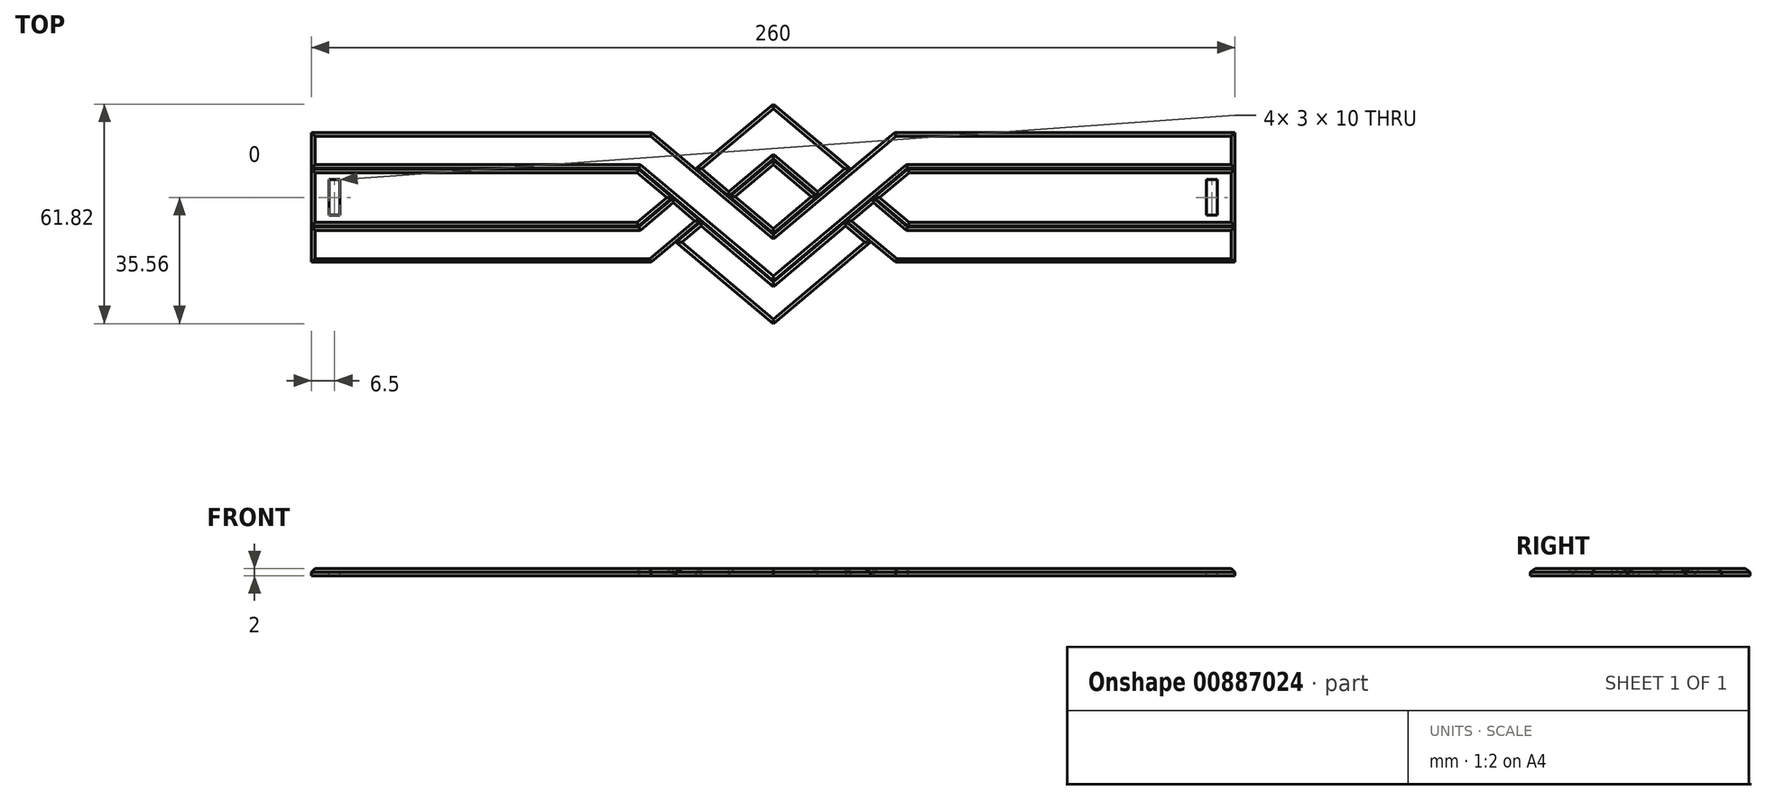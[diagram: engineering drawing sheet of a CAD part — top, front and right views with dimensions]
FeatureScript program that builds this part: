
annotation { "Feature Type Name" : "Feature", "Feature Type Description" : "" }
export const myFeature = defineFeature(function(context is Context, id is Id, definition is map)
    precondition{}
    {
        {
            var Q0;
            Q0=qCreatedBy(makeId("Top.planeOp"),FACE);
            var sketch = newSketch(context, id + "F0", { "sketchPlane" : qUnion([Q0])});
            skLineSegment(sketch, "E0", {"start": v(28.38, 0) * mm, "end": v(37.92, 8) * mm});
            skLineSegment(sketch, "E1", {"start": v(37.92, 8) * mm, "end": v(130, 8) * mm});
            skLineSegment(sketch, "E2", {"start": v(130, 8) * mm, "end": v(130, 0) * mm});
            skLineSegment(sketch, "E3.MirrorCS", {"start": v(28.38, 0) * mm, "end": v(37.92, -8) * mm});
            skLineSegment(sketch, "E4.MirrorCS", {"start": v(37.92, -8) * mm, "end": v(130, -8) * mm});
            skLineSegment(sketch, "E5.MirrorCS", {"start": v(130, -8) * mm, "end": v(130, 0) * mm});
            skLineSegment(sketch, "E6.MirrorCS", {"start": v(-28.38, 0) * mm, "end": v(-37.92, 8) * mm});
            skLineSegment(sketch, "E7.MirrorCS", {"start": v(-37.92, -8) * mm, "end": v(-130, -8) * mm});
            skLineSegment(sketch, "E8.MirrorCS", {"start": v(-28.38, 0) * mm, "end": v(-37.92, -8) * mm});
            skLineSegment(sketch, "E9.MirrorCS", {"start": v(-37.92, 8) * mm, "end": v(-130, 8) * mm});
            skLineSegment(sketch, "E10.MirrorCS", {"start": v(-130, -8) * mm, "end": v(-130, 0) * mm});
            skLineSegment(sketch, "E11.MirrorCS", {"start": v(-130, 8) * mm, "end": v(-130, 0) * mm});
            skSolve(sketch);
        }
        {
            var Q0;
            Q0 = qSketchRegion(id + "F0", true);
            extrude(context, id + "F1", {"entities" : qUnion([Q0]), "depth" : 2 * mm, "offsetDistance" : 25 * mm});
        }
        {
            var Q0;
            Q0=qCreatedBy(makeId("Top.planeOp"),FACE);
            var sketch = newSketch(context, id + "F2", { "sketchPlane" : qUnion([Q0])});
            skLineSegment(sketch, "E12", {"start": v(0, -23.49) * mm, "end": v(37.82, 8.25) * mm});
            skLineSegment(sketch, "E13", {"start": v(37.82, 8.25) * mm, "end": v(130, 8.25) * mm});
            skLineSegment(sketch, "E14", {"start": v(130, 8.25) * mm, "end": v(130, 18.25) * mm});
            skLineSegment(sketch, "E15", {"start": v(130, 18.25) * mm, "end": v(34.18, 18.25) * mm});
            skLineSegment(sketch, "E16", {"start": v(34.18, 18.25) * mm, "end": v(0, -10.43) * mm});
            skLineSegment(sketch, "E17.MirrorCS", {"start": v(-130, 8.25) * mm, "end": v(-130, 18.25) * mm});
            skLineSegment(sketch, "E18.MirrorCS", {"start": v(-130, 18.25) * mm, "end": v(-34.18, 18.25) * mm});
            skLineSegment(sketch, "E19.MirrorCS", {"start": v(0, -23.49) * mm, "end": v(-37.82, 8.25) * mm});
            skLineSegment(sketch, "E20.MirrorCS", {"start": v(-34.18, 18.25) * mm, "end": v(0, -10.43) * mm});
            skLineSegment(sketch, "E21.MirrorCS", {"start": v(-37.82, 8.25) * mm, "end": v(-130, 8.25) * mm});
            skSolve(sketch);
        }
        {
            var Q0;
            Q0 = qSketchRegion(id + "F2", true);
            extrude(context, id + "F3", {"entities" : qUnion([Q0]), "depth" : 2 * mm, "offsetDistance" : 25 * mm});
        }
        {
            var Q0;
            Q0=qCreatedBy(makeId("Top.planeOp"),FACE);
            var sketch = newSketch(context, id + "F4", { "sketchPlane" : qUnion([Q0])});
            skLineSegment(sketch, "E22", {"start": v(21.67, 8.08) * mm, "end": v(12.48, 0.37) * mm});
            skLineSegment(sketch, "E23", {"start": v(12.48, 0.37) * mm, "end": v(0, 10.84) * mm});
            skLineSegment(sketch, "E24", {"start": v(21.67, 8.08) * mm, "end": v(0, 26.26) * mm});
            skLineSegment(sketch, "E25", {"start": v(28.19, -0.16) * mm, "end": v(37.82, -8.25) * mm});
            skLineSegment(sketch, "E26", {"start": v(37.82, -8.25) * mm, "end": v(130, -8.25) * mm});
            skLineSegment(sketch, "E27", {"start": v(130, -8.25) * mm, "end": v(130, -18.25) * mm});
            skLineSegment(sketch, "E28", {"start": v(130, -18.25) * mm, "end": v(34.42, -18.25) * mm});
            skLineSegment(sketch, "E29", {"start": v(34.42, -18.25) * mm, "end": v(20.53, -6.6) * mm});
            skLineSegment(sketch, "E30", {"start": v(20.53, -6.6) * mm, "end": v(28.19, -0.16) * mm});
            skLineSegment(sketch, "E31.MirrorCS", {"start": v(-21.67, 8.08) * mm, "end": v(-12.48, 0.37) * mm});
            skLineSegment(sketch, "E32.MirrorCS", {"start": v(-21.67, 8.08) * mm, "end": v(0, 26.26) * mm});
            skLineSegment(sketch, "E33.MirrorCS", {"start": v(-12.48, 0.37) * mm, "end": v(0, 10.84) * mm});
            skLineSegment(sketch, "E34.MirrorCS", {"start": v(-34.42, -18.25) * mm, "end": v(-20.53, -6.6) * mm});
            skLineSegment(sketch, "E35.MirrorCS", {"start": v(-28.19, -0.16) * mm, "end": v(-37.82, -8.25) * mm});
            skLineSegment(sketch, "E36.MirrorCS", {"start": v(-130, -18.25) * mm, "end": v(-34.42, -18.25) * mm});
            skLineSegment(sketch, "E37.MirrorCS", {"start": v(-20.53, -6.6) * mm, "end": v(-28.19, -0.16) * mm});
            skLineSegment(sketch, "E38.MirrorCS", {"start": v(-37.82, -8.25) * mm, "end": v(-130, -8.25) * mm});
            skLineSegment(sketch, "E39.MirrorCS", {"start": v(-130, -8.25) * mm, "end": v(-130, -18.25) * mm});
            skSolve(sketch);
        }
        {
            var Q0;
            Q0 = qSketchRegion(id + "F4", true);
            extrude(context, id + "F5", {"entities" : qUnion([Q0]), "depth" : 2 * mm, "offsetDistance" : 25 * mm});
        }
        {
            var Q0;
            Q0=qCreatedBy(makeId("Top.planeOp"),FACE);
            var sketch = newSketch(context, id + "F6", { "sketchPlane" : qUnion([Q0])});
            skLineSegment(sketch, "E40", {"start": v(0, -35.56) * mm, "end": v(27.33, -12.63) * mm});
            skLineSegment(sketch, "E41", {"start": v(27.33, -12.63) * mm, "end": v(20.33, -6.75) * mm});
            skLineSegment(sketch, "E42", {"start": v(20.33, -6.75) * mm, "end": v(0, -23.81) * mm});
            skLineSegment(sketch, "E43", {"start": v(0, -10.1) * mm, "end": v(12.29, 0.2) * mm});
            skLineSegment(sketch, "E44", {"start": v(12.29, 0.2) * mm, "end": v(0, 10.51) * mm});
            skLineSegment(sketch, "E45.MirrorCS", {"start": v(-12.29, 0.2) * mm, "end": v(0, 10.51) * mm});
            skLineSegment(sketch, "E46.MirrorCS", {"start": v(0, -35.56) * mm, "end": v(-27.33, -12.63) * mm});
            skLineSegment(sketch, "E47.MirrorCS", {"start": v(0, -10.1) * mm, "end": v(-12.29, 0.2) * mm});
            skLineSegment(sketch, "E48.MirrorCS", {"start": v(-27.33, -12.63) * mm, "end": v(-20.33, -6.75) * mm});
            skLineSegment(sketch, "E49.MirrorCS", {"start": v(-20.33, -6.75) * mm, "end": v(0, -23.81) * mm});
            skSolve(sketch);
        }
        {
            var Q0;
            Q0 = qSketchRegion(id + "F6", true);
            extrude(context, id + "F7", {"entities" : qUnion([Q0]), "depth" : 2 * mm, "offsetDistance" : 25 * mm});
        }
        {
            var Q0;
            Q0=qCreatedBy(makeId("Top.planeOp"),FACE);
            var sketch = newSketch(context, id + "F8", { "sketchPlane" : qUnion([Q0])});
            skLineSegment(sketch, "E50", {"start": v(0, 26.26) * mm, "end": v(21.87, 7.92) * mm});
            skLineSegment(sketch, "E51", {"start": v(21.87, 7.92) * mm, "end": v(34.18, 18.25) * mm});
            skLineSegment(sketch, "E52", {"start": v(34.18, 18.25) * mm, "end": v(130, 18.25) * mm});
            skLineSegment(sketch, "E53", {"start": v(130, 18.25) * mm, "end": v(130, -18.25) * mm});
            skLineSegment(sketch, "E54", {"start": v(130, -18.25) * mm, "end": v(34.42, -18.25) * mm});
            skLineSegment(sketch, "E55", {"start": v(34.42, -18.25) * mm, "end": v(27.53, -12.47) * mm});
            skLineSegment(sketch, "E56", {"start": v(27.53, -12.47) * mm, "end": v(0, -35.56) * mm});
            skLineSegment(sketch, "E57.MirrorCS", {"start": v(-130, 18.25) * mm, "end": v(-130, -18.25) * mm});
            skLineSegment(sketch, "E58.MirrorCS", {"start": v(0, 26.26) * mm, "end": v(-21.87, 7.92) * mm});
            skLineSegment(sketch, "E59.MirrorCS", {"start": v(-34.18, 18.25) * mm, "end": v(-130, 18.25) * mm});
            skLineSegment(sketch, "E60.MirrorCS", {"start": v(-130, -18.25) * mm, "end": v(-34.42, -18.25) * mm});
            skLineSegment(sketch, "E61.MirrorCS", {"start": v(-34.42, -18.25) * mm, "end": v(-27.53, -12.47) * mm});
            skLineSegment(sketch, "E62.MirrorCS", {"start": v(-21.87, 7.92) * mm, "end": v(-34.18, 18.25) * mm});
            skLineSegment(sketch, "E63.MirrorCS", {"start": v(-27.53, -12.47) * mm, "end": v(0, -35.56) * mm});
            skSolve(sketch);
        }
        {
            var Q0;
            Q0 = qSketchRegion(id + "F8", true);
            extrude(context, id + "F9", {"entities" : qUnion([Q0]), "depth" : 1 * mm, "offsetDistance" : 25 * mm});
        }
        {
            var Q0;
            Q0=makeQuery(id+"F3.opExtrude","CAP_FACE",FACE,{"disambiguationData":[OSD([sQuery(id+"F2.wireOp",EDGE,"E12"),sQuery(id+"F2.wireOp",EDGE,"E13"),sQuery(id+"F2.wireOp",EDGE,"E14"),sQuery(id+"F2.wireOp",EDGE,"E15"),sQuery(id+"F2.wireOp",EDGE,"E16"),sQuery(id+"F2.wireOp",EDGE,"E17.MirrorCS"),sQuery(id+"F2.wireOp",EDGE,"E18.MirrorCS"),sQuery(id+"F2.wireOp",EDGE,"E19.MirrorCS"),sQuery(id+"F2.wireOp",EDGE,"E20.MirrorCS"),sQuery(id+"F2.wireOp",EDGE,"E21.MirrorCS")])],"isStart":false});
            var Q1;
            Q1=makeQuery(id+"F1.opExtrude","CAP_FACE",FACE,{"disambiguationData":[OSD([sQuery(id+"F0.wireOp",EDGE,"E6.MirrorCS"),sQuery(id+"F0.wireOp",EDGE,"E7.MirrorCS"),sQuery(id+"F0.wireOp",EDGE,"E8.MirrorCS"),sQuery(id+"F0.wireOp",EDGE,"E9.MirrorCS"),sQuery(id+"F0.wireOp",EDGE,"E10.MirrorCS"),sQuery(id+"F0.wireOp",EDGE,"E11.MirrorCS")])],"isStart":false});
            var Q2;
            Q2=makeQuery(id+"F5.opExtrude","CAP_FACE",FACE,{"disambiguationData":[OSD([sQuery(id+"F4.wireOp",EDGE,"E34.MirrorCS"),sQuery(id+"F4.wireOp",EDGE,"E35.MirrorCS"),sQuery(id+"F4.wireOp",EDGE,"E36.MirrorCS"),sQuery(id+"F4.wireOp",EDGE,"E37.MirrorCS"),sQuery(id+"F4.wireOp",EDGE,"E38.MirrorCS"),sQuery(id+"F4.wireOp",EDGE,"E39.MirrorCS")])],"isStart":false});
            var Q3;
            Q3=makeQuery(id+"F5.opExtrude","CAP_FACE",FACE,{"disambiguationData":[OSD([sQuery(id+"F4.wireOp",EDGE,"E22"),sQuery(id+"F4.wireOp",EDGE,"E23"),sQuery(id+"F4.wireOp",EDGE,"E24"),sQuery(id+"F4.wireOp",EDGE,"E31.MirrorCS"),sQuery(id+"F4.wireOp",EDGE,"E32.MirrorCS"),sQuery(id+"F4.wireOp",EDGE,"E33.MirrorCS")])],"isStart":false});
            var Q4;
            Q4=makeQuery(id+"F7.opExtrude","CAP_FACE",FACE,{"disambiguationData":[OSD([sQuery(id+"F6.wireOp",EDGE,"E43"),sQuery(id+"F6.wireOp",EDGE,"E44"),sQuery(id+"F6.wireOp",EDGE,"E45.MirrorCS"),sQuery(id+"F6.wireOp",EDGE,"E47.MirrorCS")])],"isStart":false});
            var Q5;
            Q5=makeQuery(id+"F7.opExtrude","CAP_FACE",FACE,{"disambiguationData":[OSD([sQuery(id+"F6.wireOp",EDGE,"E40"),sQuery(id+"F6.wireOp",EDGE,"E41"),sQuery(id+"F6.wireOp",EDGE,"E42"),sQuery(id+"F6.wireOp",EDGE,"E46.MirrorCS"),sQuery(id+"F6.wireOp",EDGE,"E48.MirrorCS"),sQuery(id+"F6.wireOp",EDGE,"E49.MirrorCS")])],"isStart":false});
            var Q6;
            Q6=makeQuery(id+"F5.opExtrude","CAP_FACE",FACE,{"disambiguationData":[OSD([sQuery(id+"F4.wireOp",EDGE,"E25"),sQuery(id+"F4.wireOp",EDGE,"E26"),sQuery(id+"F4.wireOp",EDGE,"E27"),sQuery(id+"F4.wireOp",EDGE,"E28"),sQuery(id+"F4.wireOp",EDGE,"E29"),sQuery(id+"F4.wireOp",EDGE,"E30")])],"isStart":false});
            var Q7;
            Q7=makeQuery(id+"F1.opExtrude","CAP_FACE",FACE,{"disambiguationData":[OSD([sQuery(id+"F0.wireOp",EDGE,"E0"),sQuery(id+"F0.wireOp",EDGE,"E1"),sQuery(id+"F0.wireOp",EDGE,"E2"),sQuery(id+"F0.wireOp",EDGE,"E3.MirrorCS"),sQuery(id+"F0.wireOp",EDGE,"E4.MirrorCS"),sQuery(id+"F0.wireOp",EDGE,"E5.MirrorCS")])],"isStart":false});
            chamfer(context, id + "F10", {"entities" : qUnion([Q0, Q1, Q2, Q3, Q4, Q5, Q6, Q7]), "width" : 1 * mm, "tangentPropagation" : true});
        }
        {
            var Q0;
            Q0=makeQuery(id+"F1.opExtrude","CAP_FACE",FACE,{"disambiguationData":[OSD([sQuery(id+"F0.wireOp",EDGE,"E0"),sQuery(id+"F0.wireOp",EDGE,"E1"),sQuery(id+"F0.wireOp",EDGE,"E2"),sQuery(id+"F0.wireOp",EDGE,"E3.MirrorCS"),sQuery(id+"F0.wireOp",EDGE,"E4.MirrorCS"),sQuery(id+"F0.wireOp",EDGE,"E5.MirrorCS")])],"isStart":false});
            var sketch = newSketch(context, id + "F11", { "sketchPlane" : qUnion([Q0])});
            skLineSegment(sketch, "E64.bottom", {"start": v(122, 5) * mm, "end": v(125, 5) * mm});
            skLineSegment(sketch, "E64.top", {"start": v(122, -5) * mm, "end": v(125, -5) * mm});
            skLineSegment(sketch, "E64.left", {"start": v(122, 5) * mm, "end": v(122, -5) * mm});
            skLineSegment(sketch, "E64.right", {"start": v(125, 5) * mm, "end": v(125, -5) * mm});
            skPoint(sketch, "E64.middle", {"position": v(123.5, 0) * mm});
            skLineSegment(sketch, "E65.MirrorCS", {"start": v(-122, 5) * mm, "end": v(-125, 5) * mm});
            skLineSegment(sketch, "E66.MirrorCS", {"start": v(-122, -5) * mm, "end": v(-125, -5) * mm});
            skLineSegment(sketch, "E67.MirrorCS", {"start": v(-122, 5) * mm, "end": v(-122, -5) * mm});
            skLineSegment(sketch, "E68.MirrorCS", {"start": v(-125, 5) * mm, "end": v(-125, -5) * mm});
            skPoint(sketch, "E69.MirrorP", {"position": v(-123.5, 0) * mm});
            skSolve(sketch);
        }
        {
            var Q0;
            Q0 = qSketchRegion(id + "F11", true);
            var Q1;
            Q1=makeQuery(id+"F7.boolean.opBoolean","MERGE",FACE,{"derivedFrom":[makeQuery(id+"F5.boolean.opBoolean","MERGE",FACE,{"derivedFrom":[makeQuery(id+"F3.boolean.opBoolean","MERGE",FACE,{"derivedFrom":[makeQuery(id+"F9.opExtrude","CAP_FACE",FACE,{"disambiguationData":[OSD([sQuery(id+"F8.wireOp",EDGE,"LxcJdnRJ-SJV3-MroC-tWkd-7bGJE9tuYNI7.bottom"),sQuery(id+"F8.wireOp",EDGE,"LxcJdnRJ-SJV3-MroC-tWkd-7bGJE9tuYNI7.top"),sQuery(id+"F8.wireOp",EDGE,"LxcJdnRJ-SJV3-MroC-tWkd-7bGJE9tuYNI7.left"),sQuery(id+"F8.wireOp",EDGE,"LxcJdnRJ-SJV3-MroC-tWkd-7bGJE9tuYNI7.right")])],"isStart":true}),makeQuery(id+"F3.opExtrude","CAP_FACE",FACE,{"disambiguationData":[OSD([sQuery(id+"F2.wireOp",EDGE,"E12"),sQuery(id+"F2.wireOp",EDGE,"E13"),sQuery(id+"F2.wireOp",EDGE,"E14"),sQuery(id+"F2.wireOp",EDGE,"E15"),sQuery(id+"F2.wireOp",EDGE,"E16"),sQuery(id+"F2.wireOp",EDGE,"E17.MirrorCS"),sQuery(id+"F2.wireOp",EDGE,"E18.MirrorCS"),sQuery(id+"F2.wireOp",EDGE,"E19.MirrorCS"),sQuery(id+"F2.wireOp",EDGE,"E20.MirrorCS"),sQuery(id+"F2.wireOp",EDGE,"E21.MirrorCS")])],"isStart":true})]}),makeQuery(id+"F5.opExtrude","CAP_FACE",FACE,{"disambiguationData":[OSD([sQuery(id+"F4.wireOp",EDGE,"E22"),sQuery(id+"F4.wireOp",EDGE,"E23"),sQuery(id+"F4.wireOp",EDGE,"E24"),sQuery(id+"F4.wireOp",EDGE,"E31.MirrorCS"),sQuery(id+"F4.wireOp",EDGE,"E32.MirrorCS"),sQuery(id+"F4.wireOp",EDGE,"E33.MirrorCS")])],"isStart":true}),makeQuery(id+"F5.opExtrude","CAP_FACE",FACE,{"disambiguationData":[OSD([sQuery(id+"F4.wireOp",EDGE,"E25"),sQuery(id+"F4.wireOp",EDGE,"E26"),sQuery(id+"F4.wireOp",EDGE,"E27"),sQuery(id+"F4.wireOp",EDGE,"E28"),sQuery(id+"F4.wireOp",EDGE,"E29"),sQuery(id+"F4.wireOp",EDGE,"E30")])],"isStart":true}),makeQuery(id+"F5.opExtrude","CAP_FACE",FACE,{"disambiguationData":[OSD([sQuery(id+"F4.wireOp",EDGE,"E34.MirrorCS"),sQuery(id+"F4.wireOp",EDGE,"E35.MirrorCS"),sQuery(id+"F4.wireOp",EDGE,"E36.MirrorCS"),sQuery(id+"F4.wireOp",EDGE,"E37.MirrorCS"),sQuery(id+"F4.wireOp",EDGE,"E38.MirrorCS"),sQuery(id+"F4.wireOp",EDGE,"E39.MirrorCS")])],"isStart":true})]}),makeQuery(id+"F7.opExtrude","CAP_FACE",FACE,{"disambiguationData":[OSD([sQuery(id+"F6.wireOp",EDGE,"E40"),sQuery(id+"F6.wireOp",EDGE,"E41"),sQuery(id+"F6.wireOp",EDGE,"E42"),sQuery(id+"F6.wireOp",EDGE,"E46.MirrorCS"),sQuery(id+"F6.wireOp",EDGE,"E48.MirrorCS"),sQuery(id+"F6.wireOp",EDGE,"E49.MirrorCS")])],"isStart":true}),makeQuery(id+"F7.opExtrude","CAP_FACE",FACE,{"disambiguationData":[OSD([sQuery(id+"F6.wireOp",EDGE,"E43"),sQuery(id+"F6.wireOp",EDGE,"E44"),sQuery(id+"F6.wireOp",EDGE,"E45.MirrorCS"),sQuery(id+"F6.wireOp",EDGE,"E47.MirrorCS")])],"isStart":true})]});
            extrude(context, id + "F12", {"entities" : qUnion([Q0]), "operationType" : NewBodyOperationType.REMOVE, "endBound" : BoundingType.UP_TO_SURFACE, "oppositeDirection" : true, "depth" : 25 * mm, "endBoundEntityFace" : qUnion([Q1]), "offsetDistance" : 25 * mm});
        }
    });
